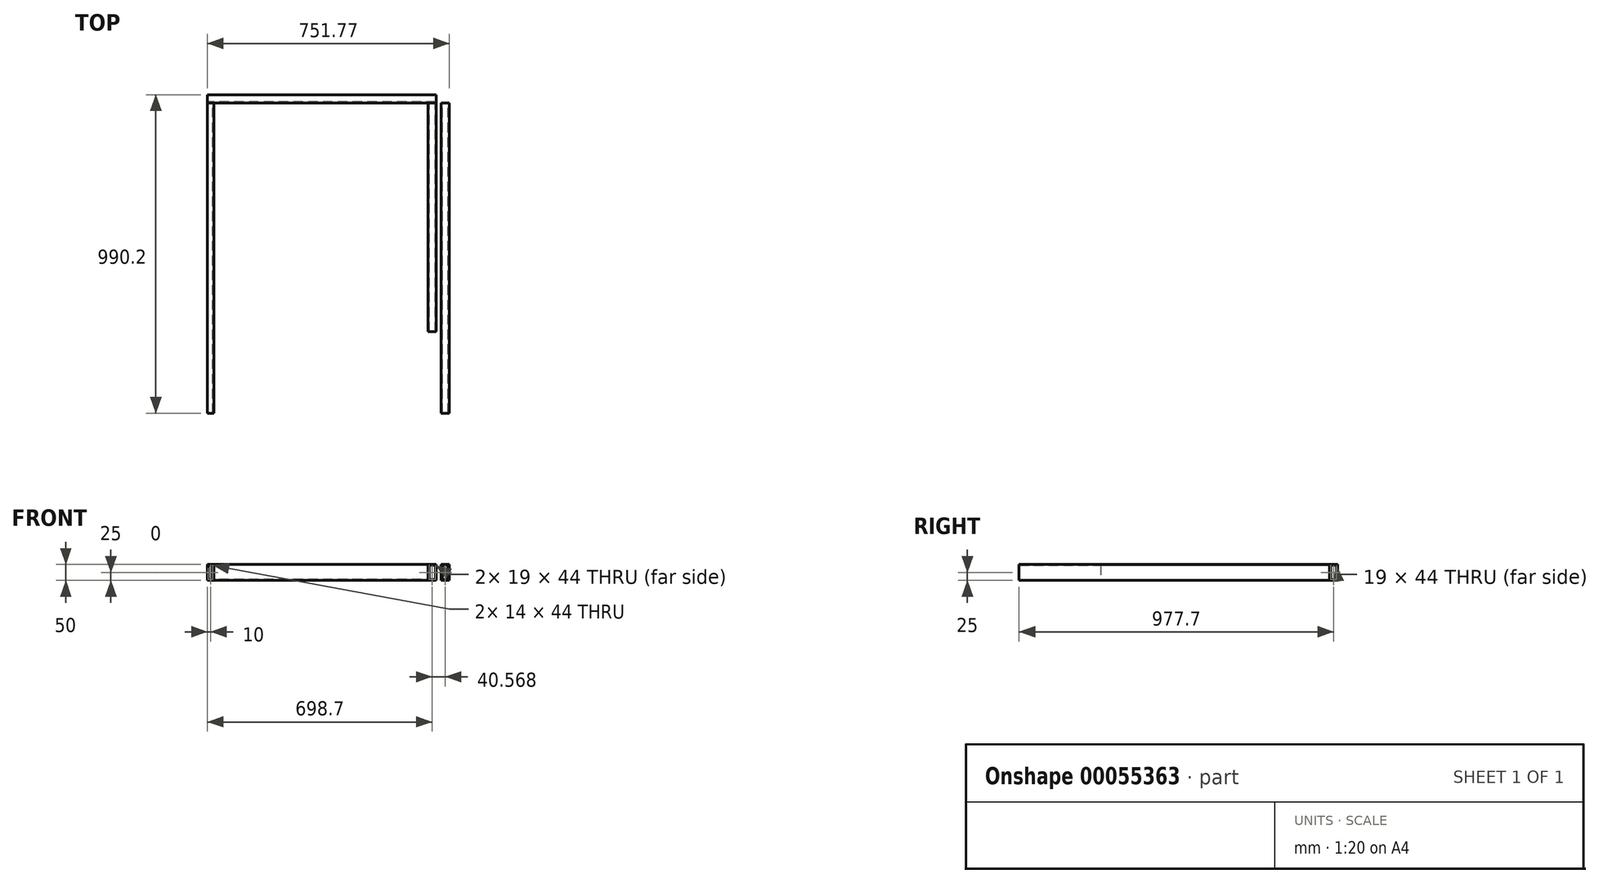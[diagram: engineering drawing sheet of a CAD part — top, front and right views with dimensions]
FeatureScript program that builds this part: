
annotation { "Feature Type Name" : "Feature", "Feature Type Description" : "" }
export const myFeature = defineFeature(function(context is Context, id is Id, definition is map)
    precondition{}
    {
        {
            var Q0;
            Q0=qCreatedBy(makeId("Front.planeOp"),FACE);
            var sketch = newSketch(context, id + "F0", { "sketchPlane" : qUnion([Q0])});
            skLineSegment(sketch, "E0.bottom", {"start": v(0, 0) * mm, "end": v(-20, 0) * mm});
            skLineSegment(sketch, "E0.top", {"start": v(0, 50) * mm, "end": v(-20, 50) * mm});
            skLineSegment(sketch, "E0.left", {"start": v(0, 0) * mm, "end": v(0, 50) * mm});
            skLineSegment(sketch, "E0.right", {"start": v(-20, 0) * mm, "end": v(-20, 50) * mm});
            skLineSegment(sketch, "E1.bottom", {"start": v(-3, 3) * mm, "end": v(-17, 3) * mm});
            skLineSegment(sketch, "E1.top", {"start": v(-3, 47) * mm, "end": v(-17, 47) * mm});
            skLineSegment(sketch, "E1.left", {"start": v(-3, 3) * mm, "end": v(-3, 47) * mm});
            skLineSegment(sketch, "E1.right", {"start": v(-17, 3) * mm, "end": v(-17, 47) * mm});
            skSolve(sketch);
        }
        {
            var Q0;
            Q0=makeQuery(id+"F0.imprint","IMPRINT",FACE,{"disambiguationData":[TD([[makeQuery(id+"F0.imprint","IMPRINT",EDGE,{"derivedFrom":sQuery(id+"F0.wireOp",EDGE,"E0.bottom")}),-1.0]])]});
            extrude(context, id + "F1", {"entities" : qUnion([Q0]), "depth" : 965.2 * mm});
        }
        {
            var Q0;
            Q0=makeQuery(id+"F1.opExtrude","SWEPT_BODY",BODY,{"disambiguationData":[OSD([sQuery(id+"F0.wireOp",EDGE,"E0.bottom"),sQuery(id+"F0.wireOp",EDGE,"E0.top"),sQuery(id+"F0.wireOp",EDGE,"E0.left"),sQuery(id+"F0.wireOp",EDGE,"E0.right"),sQuery(id+"F0.wireOp",EDGE,"E1.bottom"),sQuery(id+"F0.wireOp",EDGE,"E1.top"),sQuery(id+"F0.wireOp",EDGE,"E1.left"),sQuery(id+"F0.wireOp",EDGE,"E1.right")])]});
            transform(context, id + "F2", {"entities" : qUnion([Q0]), "transformType" : TransformType.TRANSLATION_3D, "dx" : 0 * mm, "dy" : 0 * mm, "dz" : 0 * mm, "makeCopy" : true});
        }
        {
            var Q0;
            Q0=qCreatedBy(makeId("Front.planeOp"),FACE);
            var sketch = newSketch(context, id + "F3", { "sketchPlane" : qUnion([Q0])});
            skLineSegment(sketch, "E2.bottom", {"start": v(706.77, 0) * mm, "end": v(731.77, 0) * mm});
            skLineSegment(sketch, "E2.top", {"start": v(706.77, 50) * mm, "end": v(731.77, 50) * mm});
            skLineSegment(sketch, "E2.left", {"start": v(706.77, 0) * mm, "end": v(706.77, 50) * mm});
            skLineSegment(sketch, "E2.right", {"start": v(731.77, 0) * mm, "end": v(731.77, 50) * mm});
            skLineSegment(sketch, "E3.bottom", {"start": v(709.77, 47) * mm, "end": v(728.77, 47) * mm});
            skLineSegment(sketch, "E3.top", {"start": v(709.77, 3) * mm, "end": v(728.77, 3) * mm});
            skLineSegment(sketch, "E3.left", {"start": v(709.77, 47) * mm, "end": v(709.77, 3) * mm});
            skLineSegment(sketch, "E3.right", {"start": v(728.77, 47) * mm, "end": v(728.77, 3) * mm});
            skSolve(sketch);
        }
        {
            var Q0;
            Q0 = qSketchRegion(id + "F3", true);
            extrude(context, id + "F4", {"entities" : qUnion([Q0]), "operationType" : NewBodyOperationType.ADD, "depth" : 965.2 * mm});
        }
        {
            var Q0;
            Q0=makeQuery(id+"F1.opExtrude","SWEPT_FACE",FACE,{"disambiguationData":[OSD([sQuery(id+"F0.wireOp",EDGE,"E0.right")])]});
            var sketch = newSketch(context, id + "F5", { "sketchPlane" : qUnion([Q0])});
            skLineSegment(sketch, "E4.bottom", {"start": v(0, 0) * mm, "end": v(-25, 0) * mm});
            skLineSegment(sketch, "E4.top", {"start": v(0, 50) * mm, "end": v(-25, 50) * mm});
            skLineSegment(sketch, "E4.left", {"start": v(0, 0) * mm, "end": v(0, 50) * mm});
            skLineSegment(sketch, "E4.right", {"start": v(-25, 0) * mm, "end": v(-25, 50) * mm});
            skLineSegment(sketch, "E5.bottom", {"start": v(0, 50) * mm, "end": v(0, 50) * mm});
            skLineSegment(sketch, "E5.top", {"start": v(0, 50) * mm, "end": v(0, 50) * mm});
            skLineSegment(sketch, "E5.left", {"start": v(0, 50) * mm, "end": v(0, 50) * mm});
            skLineSegment(sketch, "E5.right", {"start": v(0, 50) * mm, "end": v(0, 50) * mm});
            skLineSegment(sketch, "E6.0", {"start": v(-3, 3) * mm, "end": v(-22, 3) * mm});
            skLineSegment(sketch, "E6.1", {"start": v(-3, 3) * mm, "end": v(-3, 47) * mm});
            skLineSegment(sketch, "E6.2", {"start": v(-3, 47) * mm, "end": v(-22, 47) * mm});
            skLineSegment(sketch, "E6.3", {"start": v(-22, 3) * mm, "end": v(-22, 47) * mm});
            skSolve(sketch);
        }
        {
            var Q0;
            Q0=makeQuery(id+"F5.imprint","IMPRINT",FACE,{"disambiguationData":[TD([[makeQuery(id+"F5.imprint","IMPRINT",EDGE,{"derivedFrom":sQuery(id+"F5.wireOp",EDGE,"E4.bottom")}),-1.0]])]});
            extrude(context, id + "F6", {"entities" : qUnion([Q0]), "oppositeDirection" : true, "depth" : 711.2 * mm});
        }
        {
            var Q0;
            Q0=makeQuery(id+"F6.opExtrude","SWEPT_FACE",FACE,{"disambiguationData":[OSD([sQuery(id+"F5.wireOp",EDGE,"E4.left")])]});
            var sketch = newSketch(context, id + "F7", { "sketchPlane" : qUnion([Q0])});
            skLineSegment(sketch, "E7.bottom", {"start": v(691.2, 50) * mm, "end": v(666.2, 50) * mm});
            skLineSegment(sketch, "E7.top", {"start": v(691.2, 0) * mm, "end": v(666.2, 0) * mm});
            skLineSegment(sketch, "E7.left", {"start": v(691.2, 50) * mm, "end": v(691.2, 0) * mm});
            skLineSegment(sketch, "E7.right", {"start": v(666.2, 50) * mm, "end": v(666.2, 0) * mm});
            skLineSegment(sketch, "E8.bottom", {"start": v(669.2, 47) * mm, "end": v(688.2, 47) * mm});
            skLineSegment(sketch, "E8.top", {"start": v(669.2, 3) * mm, "end": v(688.2, 3) * mm});
            skLineSegment(sketch, "E8.left", {"start": v(669.2, 47) * mm, "end": v(669.2, 3) * mm});
            skLineSegment(sketch, "E8.right", {"start": v(688.2, 47) * mm, "end": v(688.2, 3) * mm});
            skSolve(sketch);
        }
        {
            var Q0;
            Q0 = qSketchRegion(id + "F7", true);
            extrude(context, id + "F8", {"entities" : qUnion([Q0]), "depth" : 711.2 * mm});
        }
    });
